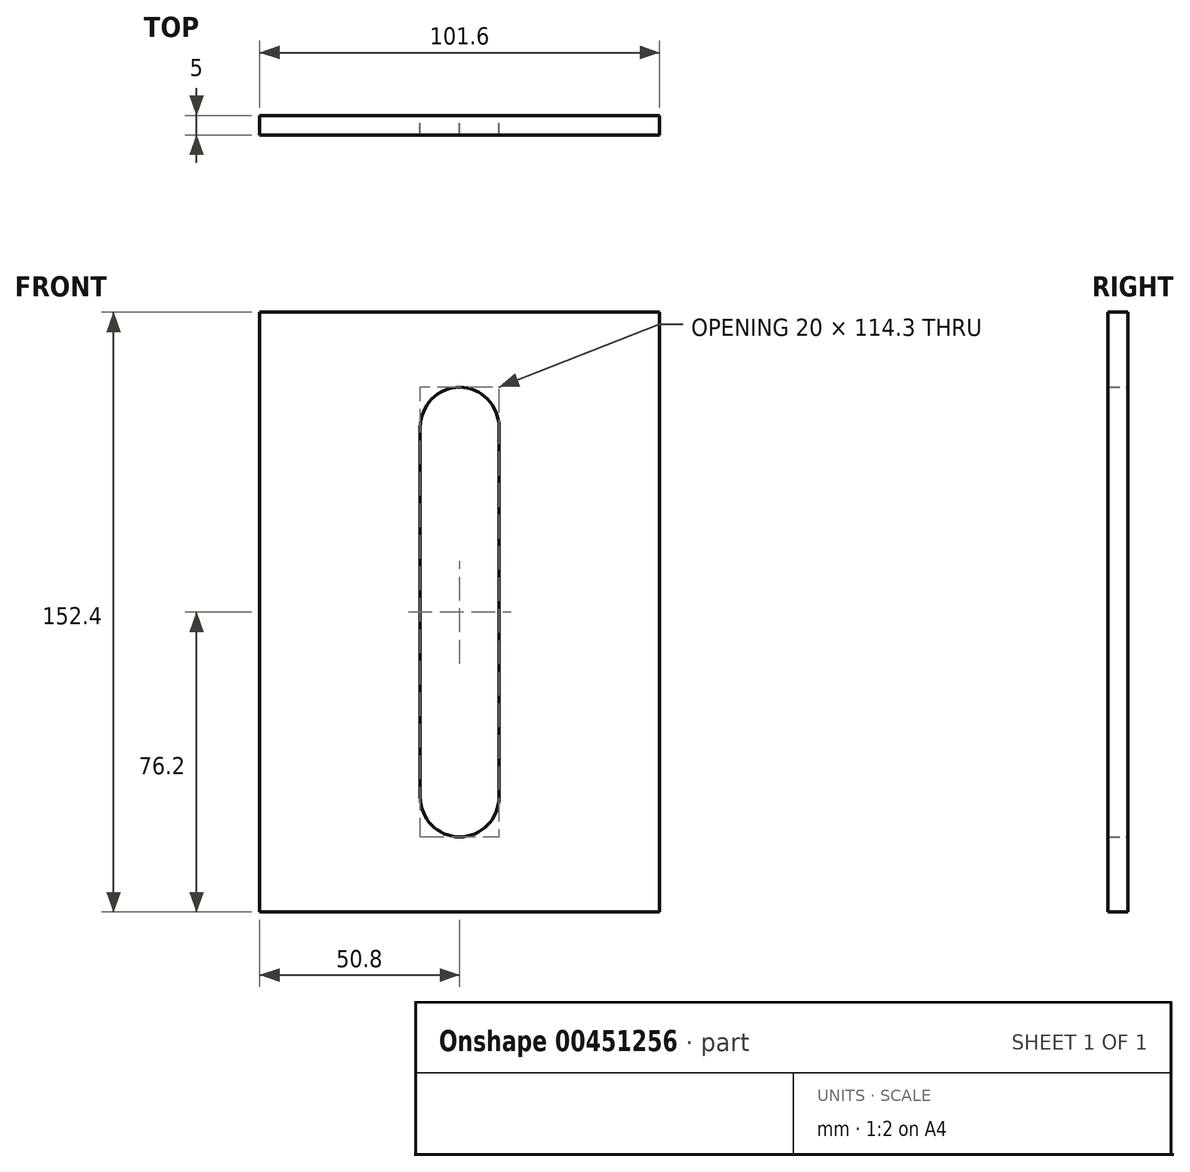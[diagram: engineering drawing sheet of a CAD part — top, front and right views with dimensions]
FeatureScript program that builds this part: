
annotation { "Feature Type Name" : "Feature", "Feature Type Description" : "" }
export const myFeature = defineFeature(function(context is Context, id is Id, definition is map)
    precondition{}
    {
        {
            var Q0;
            Q0=qCreatedBy(makeId("Front.planeOp"),FACE);
            var sketch = newSketch(context, id + "F0", { "sketchPlane" : qUnion([Q0])});
            skLineSegment(sketch, "E0.bottom", {"start": v(50.8, -76.2) * mm, "end": v(-50.8, -76.2) * mm});
            skLineSegment(sketch, "E0.top", {"start": v(50.8, 76.2) * mm, "end": v(-50.8, 76.2) * mm});
            skLineSegment(sketch, "E0.left", {"start": v(50.8, -76.2) * mm, "end": v(50.8, 76.2) * mm});
            skLineSegment(sketch, "E0.right", {"start": v(-50.8, -76.2) * mm, "end": v(-50.8, 76.2) * mm});
            skPoint(sketch, "E0.middle", {"position": v(0, 0) * mm});
            skLineSegment(sketch, "E1.bottom", {"start": v(10, -57.15) * mm, "end": v(-10, -57.15) * mm});
            skLineSegment(sketch, "E1.top", {"start": v(10, 57.15) * mm, "end": v(-10, 57.15) * mm});
            skLineSegment(sketch, "E1.left", {"start": v(10, -57.15) * mm, "end": v(10, 57.15) * mm});
            skLineSegment(sketch, "E1.right", {"start": v(-10, -57.15) * mm, "end": v(-10, 57.15) * mm});
            skSolve(sketch);
        }
        {
            var Q0;
            Q0=makeQuery(id+"F0.imprint","IMPRINT",FACE,{"disambiguationData":[TD([[makeQuery(id+"F0.imprint","IMPRINT",EDGE,{"derivedFrom":sQuery(id+"F0.wireOp",EDGE,"E0.bottom")}),-1.0]])]});
            extrude(context, id + "F1", {"entities" : qUnion([Q0]), "depth" : 5 * mm});
        }
        {
            var Q0;
            Q0=makeQuery(id+"F1.opExtrude","SWEPT_EDGE",EDGE,{"disambiguationData":[OSD([sQuery(id+"F0.wireOp",EDGE,"E1.top"),sQuery(id+"F0.wireOp",EDGE,"E1.right")])]});
            var Q1;
            Q1=makeQuery(id+"F1.opExtrude","SWEPT_EDGE",EDGE,{"disambiguationData":[OSD([sQuery(id+"F0.wireOp",EDGE,"E1.top"),sQuery(id+"F0.wireOp",EDGE,"E1.left")])]});
            var Q2;
            Q2=makeQuery(id+"F1.opExtrude","SWEPT_EDGE",EDGE,{"disambiguationData":[OSD([sQuery(id+"F0.wireOp",EDGE,"E1.bottom"),sQuery(id+"F0.wireOp",EDGE,"E1.left")])]});
            var Q3;
            Q3=makeQuery(id+"F1.opExtrude","SWEPT_EDGE",EDGE,{"disambiguationData":[OSD([sQuery(id+"F0.wireOp",EDGE,"E1.bottom"),sQuery(id+"F0.wireOp",EDGE,"E1.right")])]});
            fillet(context, id + "F2", {"entities" : qUnion([Q0, Q1, Q2, Q3]), "radius" : 10.16 * mm, "tangentPropagation" : true, "allowEdgeOverflow" : false});
        }
    });
